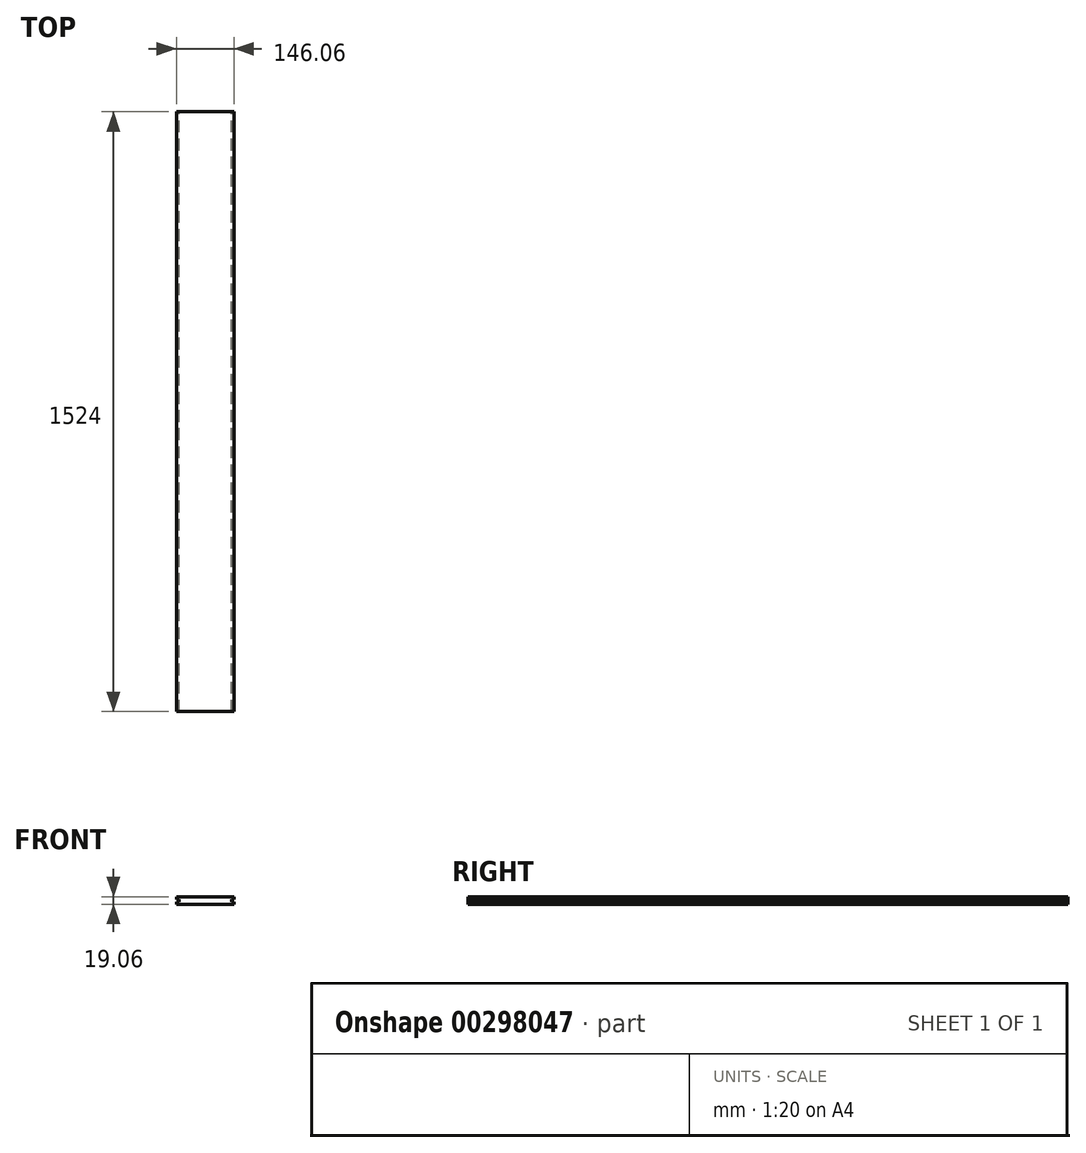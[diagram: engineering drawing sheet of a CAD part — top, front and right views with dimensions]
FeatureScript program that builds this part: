
annotation { "Feature Type Name" : "Feature", "Feature Type Description" : "" }
export const myFeature = defineFeature(function(context is Context, id is Id, definition is map)
    precondition{}
    {
        {
            var Q0;
            Q0=qCreatedBy(makeId("Front.planeOp"),FACE);
            var sketch = newSketch(context, id + "F0", { "sketchPlane" : qUnion([Q0])});
            skLineSegment(sketch, "E0.bottom", {"start": v(-73.03, -9.53) * mm, "end": v(73.03, -9.53) * mm});
            skLineSegment(sketch, "E0.top", {"start": v(-73.03, 9.52) * mm, "end": v(73.03, 9.52) * mm});
            skLineSegment(sketch, "E0.left", {"start": v(-73.03, -9.53) * mm, "end": v(-73.03, 9.53) * mm});
            skLineSegment(sketch, "E0.right", {"start": v(73.03, -9.53) * mm, "end": v(73.03, 9.53) * mm});
            skPoint(sketch, "E0.middle", {"position": v(0, 0) * mm});
            skLineSegment(sketch, "E1.bottom", {"start": v(-73.03, 3.18) * mm, "end": v(-66.68, 3.18) * mm});
            skLineSegment(sketch, "E1.top", {"start": v(-73.03, -3.17) * mm, "end": v(-66.68, -3.17) * mm});
            skLineSegment(sketch, "E1.left", {"start": v(-73.03, 3.18) * mm, "end": v(-73.03, -3.17) * mm});
            skLineSegment(sketch, "E1.right", {"start": v(-66.68, 3.18) * mm, "end": v(-66.68, -3.17) * mm});
            skPoint(sketch, "E1.middle", {"position": v(-69.85, 0) * mm});
            skLineSegment(sketch, "E2.bottom", {"start": v(73.03, 3.18) * mm, "end": v(66.67, 3.18) * mm});
            skLineSegment(sketch, "E2.top", {"start": v(73.02, -3.17) * mm, "end": v(66.67, -3.17) * mm});
            skLineSegment(sketch, "E2.left", {"start": v(73.03, 3.18) * mm, "end": v(73.03, -3.17) * mm});
            skLineSegment(sketch, "E2.right", {"start": v(66.67, 3.18) * mm, "end": v(66.67, -3.17) * mm});
            skPoint(sketch, "E2.middle", {"position": v(69.85, 0) * mm});
            skSolve(sketch);
        }
        {
            var Q0;
            {var subQ6=sQuery(id+"F0.wireOp",EDGE,"E0.bottom");Q0=makeQuery(id+"F0.imprint","IMPRINT",FACE,{"disambiguationData":[TD([[makeQuery(id+"F0.imprint","IMPRINT",EDGE,{"derivedFrom":subQ6}),1.0]])]});}
            extrude(context, id + "F1", {"entities" : qUnion([Q0]), "endBound" : BoundingType.SYMMETRIC, "depth" : 1524 * mm});
        }
    });
